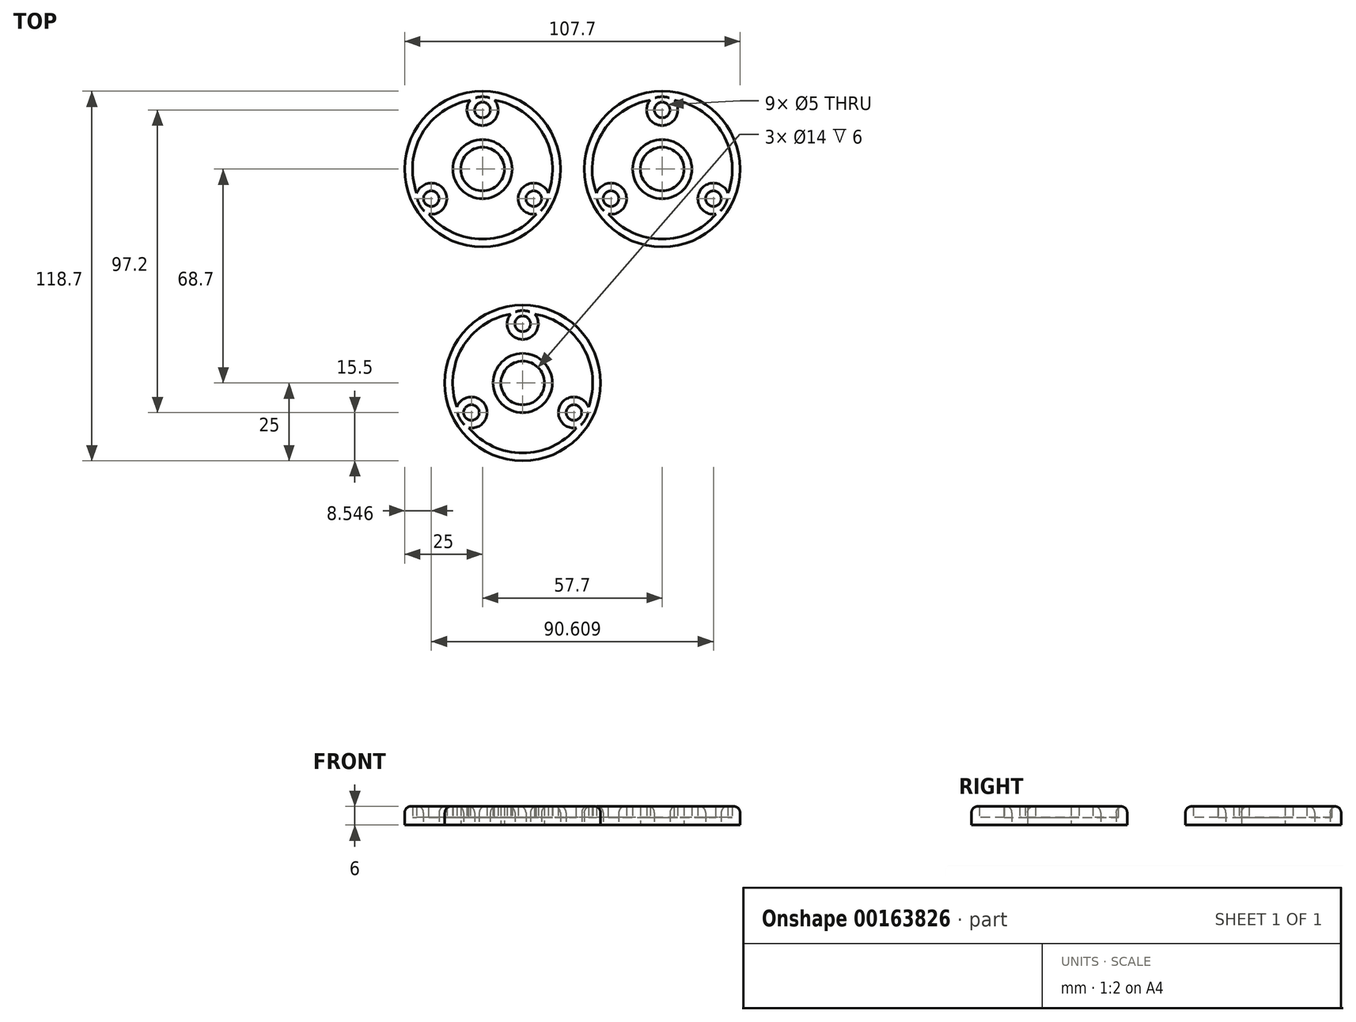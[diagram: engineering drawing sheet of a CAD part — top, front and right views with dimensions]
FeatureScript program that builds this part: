
annotation { "Feature Type Name" : "Feature", "Feature Type Description" : "" }
export const myFeature = defineFeature(function(context is Context, id is Id, definition is map)
    precondition{}
    {
        {
            var Q0;
            Q0=qCreatedBy(makeId("Top.planeOp"),FACE);
            var sketch = newSketch(context, id + "F0", { "sketchPlane" : qUnion([Q0])});
            skCircle(sketch, "E0", {"center": v(0, 0) * mm, "radius": 25 * mm});
            skCircle(sketch, "E1", {"center": v(0, 0) * mm, "radius": 7 * mm});
            skCircle(sketch, "E2", {"center": v(-16.45, -9.5) * mm, "radius": 2.5 * mm});
            skCircle(sketch, "E3", {"center": v(16.45, -9.5) * mm, "radius": 2.5 * mm});
            skCircle(sketch, "E4", {"center": v(0, 19) * mm, "radius": 2.5 * mm});
            skSolve(sketch);
        }
        {
            var Q0;
            Q0=makeQuery(id+"F0.imprint","IMPRINT",FACE,{"disambiguationData":[TD([[makeQuery(id+"F0.imprint","IMPRINT",EDGE,{"derivedFrom":sQuery(id+"F0.wireOp",EDGE,"E0")}),1.0]])]});
            extrude(context, id + "F1", {"entities" : qUnion([Q0]), "depth" : 6 * mm});
        }
        {
            var Q0;
            Q0=makeQuery(id+"F1.opExtrude","CAP_EDGE",EDGE,{"disambiguationData":[OSD([sQuery(id+"F0.wireOp",EDGE,"E0")])],"isStart":false});
            var Q1;
            Q1=makeQuery(id+"F1.opExtrude","CAP_EDGE",EDGE,{"disambiguationData":[OSD([sQuery(id+"F0.wireOp",EDGE,"E3")])],"isStart":false});
            var Q2;
            Q2=makeQuery(id+"F1.opExtrude","CAP_EDGE",EDGE,{"disambiguationData":[OSD([sQuery(id+"F0.wireOp",EDGE,"E4")])],"isStart":false});
            var Q3;
            Q3=makeQuery(id+"F1.opExtrude","CAP_EDGE",EDGE,{"disambiguationData":[OSD([sQuery(id+"F0.wireOp",EDGE,"E2")])],"isStart":false});
            fillet(context, id + "F2", {"entities" : qUnion([Q0, Q1, Q2, Q3]), "radius" : 2 * mm, "tangentPropagation" : true, "allowEdgeOverflow" : false});
        }
        {
            var Q0;
            Q0=makeQuery(id+"F1.opExtrude","CAP_FACE",FACE,{"disambiguationData":[OSD([sQuery(id+"F0.wireOp",EDGE,"E0"),sQuery(id+"F0.wireOp",EDGE,"E1"),sQuery(id+"F0.wireOp",EDGE,"E2"),sQuery(id+"F0.wireOp",EDGE,"E3"),sQuery(id+"F0.wireOp",EDGE,"E4")])],"isStart":false});
            shell(context, id + "F3", {"entities" : qUnion([Q0]), "thickness" : 2.5 * mm});
        }
        {
            var Q0;
            Q0=makeQuery(id+"F1.opExtrude","SWEPT_BODY",BODY,{"disambiguationData":[OSD([sQuery(id+"F0.wireOp",EDGE,"E0"),sQuery(id+"F0.wireOp",EDGE,"E1"),sQuery(id+"F0.wireOp",EDGE,"E2"),sQuery(id+"F0.wireOp",EDGE,"E3"),sQuery(id+"F0.wireOp",EDGE,"E4")])]});
            transform(context, id + "F4", {"entities" : qUnion([Q0]), "transformType" : TransformType.TRANSLATION_3D, "dx" : -57.7 * mm, "dy" : 0 * mm, "dz" : 0 * mm, "makeCopy" : true});
        }
        {
            var Q0;
            Q0=makeQuery(id+"F4.opPattern","COPY",BODY,{"derivedFrom":makeQuery(id+"F1.opExtrude","SWEPT_BODY",BODY,{"disambiguationData":[OSD([sQuery(id+"F0.wireOp",EDGE,"E0"),sQuery(id+"F0.wireOp",EDGE,"E1"),sQuery(id+"F0.wireOp",EDGE,"E2"),sQuery(id+"F0.wireOp",EDGE,"E3"),sQuery(id+"F0.wireOp",EDGE,"E4")])]}),"instanceName":"1"});
            transform(context, id + "F5", {"entities" : qUnion([Q0]), "transformType" : TransformType.TRANSLATION_3D, "dx" : 12.9 * mm, "dy" : -68.7 * mm, "dz" : 0 * mm, "makeCopy" : true});
        }
    });
